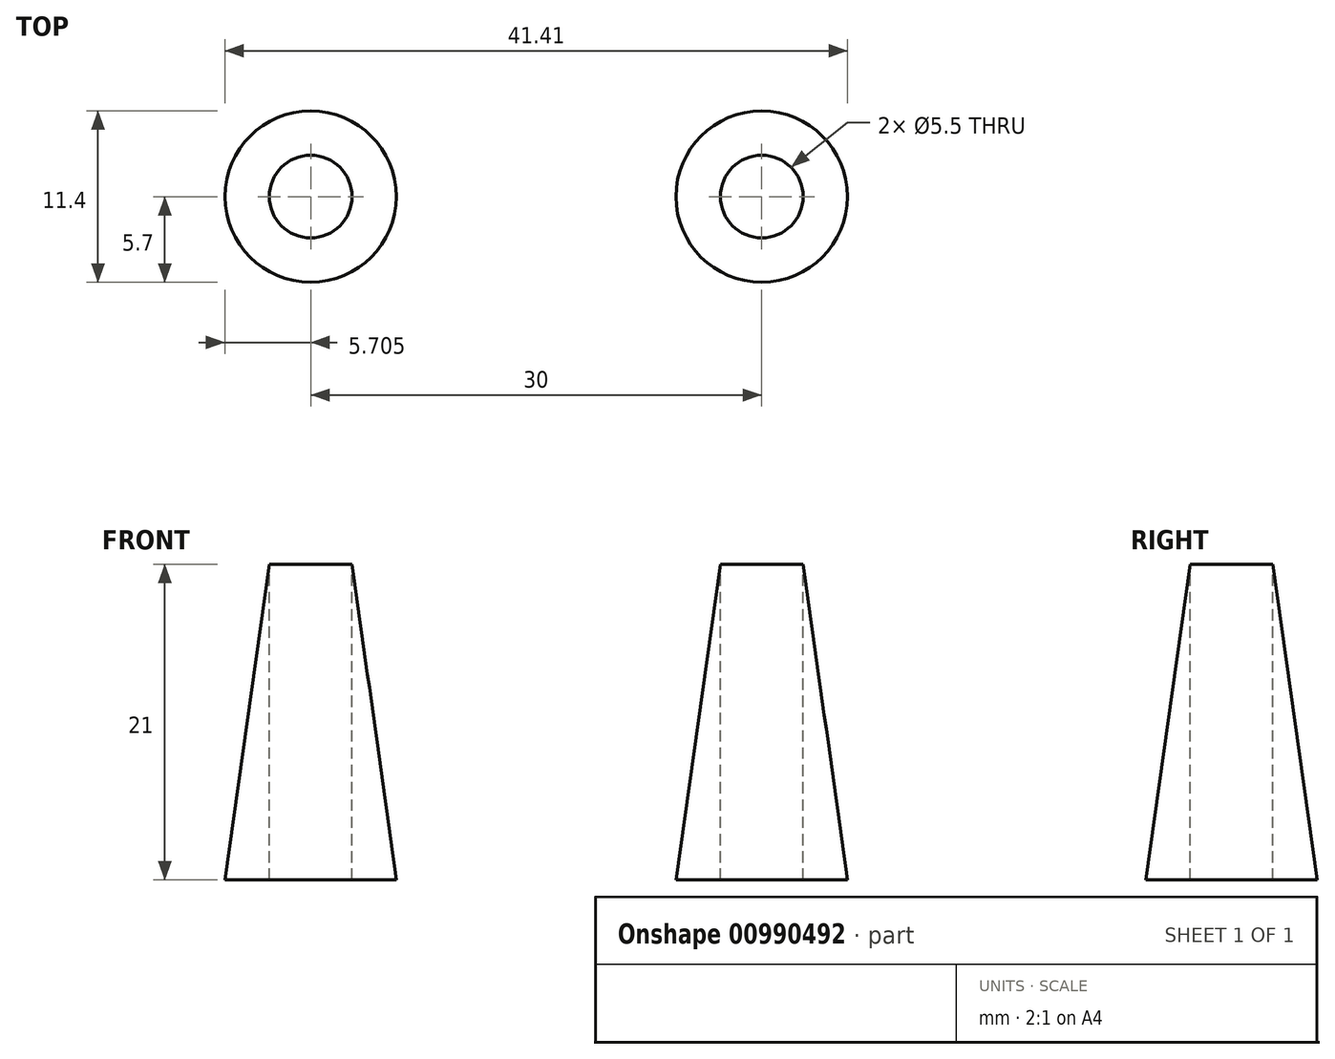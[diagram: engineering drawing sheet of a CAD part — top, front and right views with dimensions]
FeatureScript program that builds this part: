
annotation { "Feature Type Name" : "Feature", "Feature Type Description" : "" }
export const myFeature = defineFeature(function(context is Context, id is Id, definition is map)
    precondition{}
    {
        {
            var Q0;
            Q0=qCreatedBy(makeId("Top.planeOp"),FACE);
            var sketch = newSketch(context, id + "F0", { "sketchPlane" : qUnion([Q0])});
            skArc(sketch, "E0", {"start": v(15.25, 7) * mm, "mid": v(21.75, 0) * mm, "end": v(15.25, -7) * mm});
            skLineSegment(sketch, "E1", {"start": v(0, 0) * mm, "end": v(-21.75, 0) * mm, "construction": true});
            skLineSegment(sketch, "E2", {"start": v(0, 0) * mm, "end": v(21.75, 0) * mm, "construction": true});
            skLineSegment(sketch, "E3", {"start": v(-14.75, 7) * mm, "end": v(15.25, 7) * mm});
            skLineSegment(sketch, "E4", {"start": v(-14.75, -7) * mm, "end": v(15.25, -7) * mm});
            skLineSegment(sketch, "E5", {"start": v(15.25, 7) * mm, "end": v(15.25, -7) * mm, "construction": true});
            skLineSegment(sketch, "E6", {"start": v(-14.75, 7) * mm, "end": v(-14.75, 0) * mm, "construction": true});
            skLineSegment(sketch, "E7", {"start": v(-14.75, -7) * mm, "end": v(-14.75, 0) * mm, "construction": true});
            skArc(sketch, "E8", {"start": v(-14.75, -7) * mm, "mid": v(-21.75, 0) * mm, "end": v(-14.75, 7) * mm});
            skCircle(sketch, "E9", {"center": v(15.25, 0) * mm, "radius": 2.75 * mm});
            skCircle(sketch, "E10", {"center": v(-14.75, 0) * mm, "radius": 2.75 * mm});
            skSolve(sketch);
        }
        {
            var Q0;
            Q0=makeQuery(id+"F0.imprint","IMPRINT",FACE,{"disambiguationData":[TD([[makeQuery(id+"F0.imprint","IMPRINT",EDGE,{"derivedFrom":sQuery(id+"F0.wireOp",EDGE,"E0")}),-1.0]])]});
            var Q1;
            Q1=makeQuery(id+"F0.imprint","IMPRINT",FACE,{"disambiguationData":[TD([[makeQuery(id+"F0.imprint","IMPRINT",EDGE,{"derivedFrom":sQuery(id+"F0.wireOp",EDGE,"E9")}),1.0]])]});
            var Q2;
            Q2=makeQuery(id+"F0.imprint","IMPRINT",FACE,{"disambiguationData":[TD([[makeQuery(id+"F0.imprint","IMPRINT",EDGE,{"derivedFrom":sQuery(id+"F0.wireOp",EDGE,"E10")}),1.0]])]});
            extrude(context, id + "F1", {"entities" : qUnion([Q0, Q1, Q2]), "oppositeDirection" : true, "depth" : 21 * mm, "offsetDistance" : 25 * mm, "hasDraft" : true, "draftAngle" : 8 * degree});
        }
        {
            var Q0;
            Q0=makeQuery(id+"F0.imprint","IMPRINT",FACE,{"disambiguationData":[TD([[makeQuery(id+"F0.imprint","IMPRINT",EDGE,{"derivedFrom":sQuery(id+"F0.wireOp",EDGE,"E9")}),1.0]])]});
            var Q1;
            Q1=makeQuery(id+"F0.imprint","IMPRINT",FACE,{"disambiguationData":[TD([[makeQuery(id+"F0.imprint","IMPRINT",EDGE,{"derivedFrom":sQuery(id+"F0.wireOp",EDGE,"E10")}),1.0]])]});
            extrude(context, id + "F2", {"entities" : qUnion([Q0, Q1]), "operationType" : NewBodyOperationType.REMOVE, "endBound" : BoundingType.THROUGH_ALL, "oppositeDirection" : true, "depth" : 25 * mm, "offsetDistance" : 25 * mm});
        }
    });
